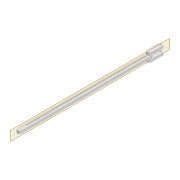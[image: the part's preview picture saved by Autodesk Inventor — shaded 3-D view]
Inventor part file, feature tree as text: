
AUTODESK INVENTOR PART (.ipt)
format: ipt  version: 2022 (Build 260153000, 153)  size: 151,552 bytes
history: native  units: mm
features: extrude x6, sketch x5, projected_geometry x4
ambient origin geometry x8: Origin, YZ Plane, XZ Plane, XY Plane, X Axis, Y Axis, Z Axis, Center Point
bodies: Solid1 (feature_tree)
feature tree (15):
  extrude  "Extrusion1"  Depth=6.0mm
  sketch  "Sketch2"  dims[d3=189.937mm d6=4.0mm d7=0.0mm]
  extrude  "Extrusion2"  Depth=4.0mm TaperAngle=0.0deg
  extrude  "Extrusion3"  Depth=2.2mm
  extrude  "Extrusion4"  Depth=10.0mm
  extrude  "Extrusion5"  Depth=4.0mm TaperAngle=0.0deg
  extrude  "Extrusion6"  Depth=6.0mm
  sketch  "Sketch1"  dims[d1=2.2mm d2=6.0mm]
  projected_geometry  "Projected Loop1"
  sketch  "Sketch3"  dims[d16=2.2mm d17=20.0mm]
  projected_geometry  "Projected Loop2"
  sketch  "Sketch4"  dims[d18=10.0mm d20=15.0mm]
  projected_geometry  "Projected Loop3"
  sketch  "Sketch5"  dims[d21=6.0mm d22=4.0mm d23=0.0mm d24=6.0mm d25=15.0mm d26=4.0mm d27=0.0mm d28=4.0mm d29=0.0mm d30=0.2mm d31=0.0mm d32=0.2mm d33=0.0mm]
  projected_geometry  "Projected Loop4"
